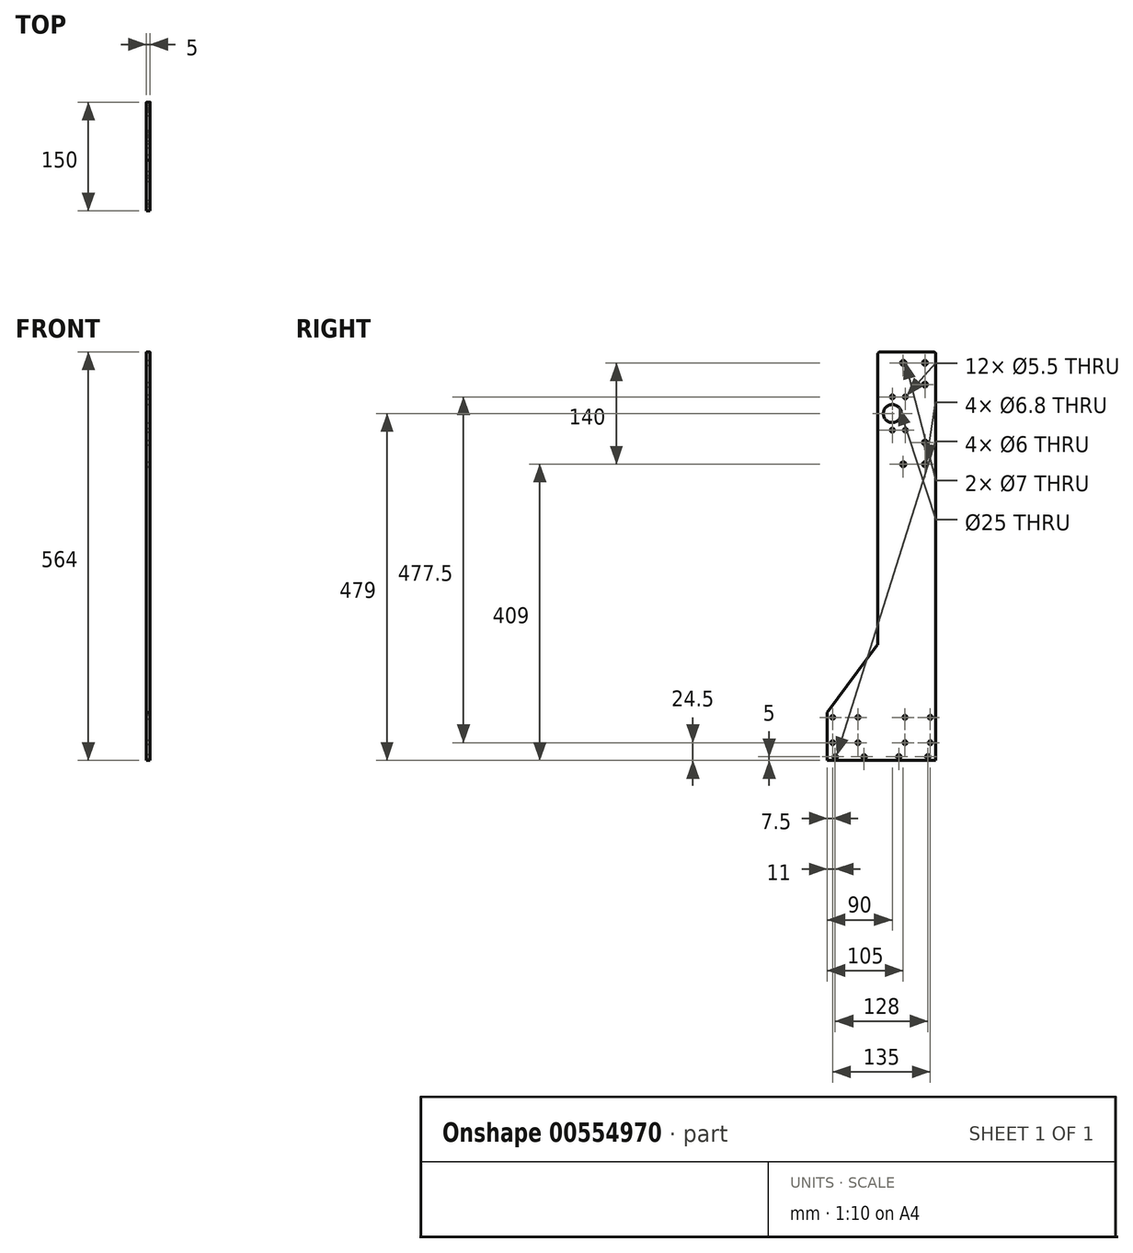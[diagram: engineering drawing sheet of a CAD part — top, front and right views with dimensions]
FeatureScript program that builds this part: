
annotation { "Feature Type Name" : "Feature", "Feature Type Description" : "" }
export const myFeature = defineFeature(function(context is Context, id is Id, definition is map)
    precondition{}
    {
        {
            var Q0;
            Q0=qCreatedBy(makeId("Right.planeOp"),FACE);
            var sketch = newSketch(context, id + "F0", { "sketchPlane" : qUnion([Q0])});
            skLineSegment(sketch, "E0.bottom", {"start": v(40, 282) * mm, "end": v(-40, 282) * mm});
            skLineSegment(sketch, "E0.top", {"start": v(40, -282) * mm, "end": v(-40, -282) * mm});
            skLineSegment(sketch, "E0.left", {"start": v(40, 282) * mm, "end": v(40, -282) * mm});
            skLineSegment(sketch, "E0.right", {"start": v(-40, 282) * mm, "end": v(-40, -122) * mm});
            skPoint(sketch, "E0.middle", {"position": v(0, 0) * mm});
            skLineSegment(sketch, "E1", {"start": v(-40, -282) * mm, "end": v(-110, -282) * mm});
            skLineSegment(sketch, "E2", {"start": v(-110, -282) * mm, "end": v(-110, -216) * mm});
            skLineSegment(sketch, "E3", {"start": v(-40, -122) * mm, "end": v(-110, -216) * mm});
            skSolve(sketch);
        }
        {
            var Q0;
            Q0=qSketchRegion(id+"F0",true);
            extrude(context, id + "F1", {"entities" : qUnion([Q0]), "endBound" : BoundingType.SYMMETRIC, "depth" : 5 * mm, "offsetDistance" : 25 * mm});
        }
        {
            var Q0;
            Q0=makeQuery(id+"F1.opExtrude","CAP_FACE",FACE,{"disambiguationData":[OSD([sQuery(id+"F0.wireOp",EDGE,"E0.bottom"),sQuery(id+"F0.wireOp",EDGE,"E0.top"),sQuery(id+"F0.wireOp",EDGE,"E0.left"),sQuery(id+"F0.wireOp",EDGE,"E0.right")])],"isStart":false});
            var sketch = newSketch(context, id + "F2", { "sketchPlane" : qUnion([Q0])});
            skCircle(sketch, "E4", {"center": v(25, 267) * mm, "radius": 3.4 * mm});
            skCircle(sketch, "E5", {"center": v(25, 237) * mm, "radius": 3.4 * mm});
            skCircle(sketch, "E6", {"center": v(25, 127) * mm, "radius": 3.4 * mm});
            skCircle(sketch, "E7", {"center": v(25, 157) * mm, "radius": 3.4 * mm});
            skCircle(sketch, "E8", {"center": v(-5, 267) * mm, "radius": 3.5 * mm});
            skCircle(sketch, "E9", {"center": v(-5, 127) * mm, "radius": 3.5 * mm});
            skCircle(sketch, "E10", {"center": v(-20, 197) * mm, "radius": 12.5 * mm});
            skPoint(sketch, "E11.center.orphan", {"position": v(-5, 237) * mm});
            skPoint(sketch, "E12.center.orphan", {"position": v(-5, 157) * mm});
            skCircle(sketch, "E13", {"center": v(-20, 220) * mm, "radius": 2.75 * mm});
            skCircle(sketch, "E14", {"center": v(-2, 220) * mm, "radius": 2.75 * mm});
            skCircle(sketch, "E15", {"center": v(-20, 174) * mm, "radius": 2.75 * mm});
            skCircle(sketch, "E16", {"center": v(-2, 174) * mm, "radius": 2.75 * mm});
            skSolve(sketch);
        }
        {
            var Q0;
            Q0=qSketchRegion(id+"F2",true);
            extrude(context, id + "F3", {"entities" : qUnion([Q0]), "operationType" : NewBodyOperationType.REMOVE, "oppositeDirection" : true, "depth" : 5 * mm, "offsetDistance" : 25 * mm});
        }
        {
            var Q0;
            Q0=makeQuery(id+"F1.opExtrude","SWEPT_EDGE",EDGE,{"disambiguationData":[OSD([sQuery(id+"F0.wireOp",EDGE,"E0.bottom"),sQuery(id+"F0.wireOp",EDGE,"E0.left")])]});
            fillet(context, id + "F4", {"entities" : qUnion([Q0]), "radius" : 3 * mm, "tangentPropagation" : true, "allowEdgeOverflow" : false});
        }
        {
            var Q0;
            Q0=makeQuery(id+"F1.opExtrude","SWEPT_EDGE",EDGE,{"disambiguationData":[OSD([sQuery(id+"F0.wireOp",EDGE,"E0.bottom"),sQuery(id+"F0.wireOp",EDGE,"E0.right")])]});
            fillet(context, id + "F5", {"entities" : qUnion([Q0]), "radius" : 3 * mm, "tangentPropagation" : true, "allowEdgeOverflow" : false});
        }
        {
            var Q0;
            Q0=makeQuery(id+"F1.opExtrude","SWEPT_EDGE",EDGE,{"disambiguationData":[OSD([sQuery(id+"F0.wireOp",EDGE,"E0.right"),sQuery(id+"F0.wireOp",EDGE,"1vJYxwGC-FJZn-p96J-PcUk-pM6sYgkwKhBf")])]});
            var Q1;
            Q1=makeQuery(id+"F1.opExtrude","SWEPT_EDGE",EDGE,{"disambiguationData":[OSD([sQuery(id+"F0.wireOp",EDGE,"1vJYxwGC-FJZn-p96J-PcUk-pM6sYgkwKhBf"),sQuery(id+"F0.wireOp",EDGE,"8exz0xhX-NDQy-IiUF-ustv-eXDvUxwHRywJ")])]});
            fillet(context, id + "F6", {"entities" : qUnion([Q0, Q1]), "radius" : 3 * mm, "tangentPropagation" : true, "allowEdgeOverflow" : false});
        }
        {
            var Q0;
            Q0=makeQuery(id+"F1.opExtrude","CAP_FACE",FACE,{"disambiguationData":[OSD([sQuery(id+"F0.wireOp",EDGE,"E0.bottom"),sQuery(id+"F0.wireOp",EDGE,"E0.top"),sQuery(id+"F0.wireOp",EDGE,"E0.left"),sQuery(id+"F0.wireOp",EDGE,"E0.right"),sQuery(id+"F0.wireOp",EDGE,"E1"),sQuery(id+"F0.wireOp",EDGE,"1vJYxwGC-FJZn-p96J-PcUk-pM6sYgkwKhBf"),sQuery(id+"F0.wireOp",EDGE,"E2"),sQuery(id+"F0.wireOp",EDGE,"8exz0xhX-NDQy-IiUF-ustv-eXDvUxwHRywJ")])],"isStart":true});
            var sketch = newSketch(context, id + "F7", { "sketchPlane" : qUnion([Q0])});
            skCircle(sketch, "E17", {"center": v(-29, -277) * mm, "radius": 3 * mm});
            skCircle(sketch, "E18", {"center": v(11, -277) * mm, "radius": 3 * mm});
            skCircle(sketch, "E19", {"center": v(59, -277) * mm, "radius": 3 * mm});
            skCircle(sketch, "E20", {"center": v(99, -277) * mm, "radius": 3 * mm});
            skSolve(sketch);
        }
        {
            var Q0;
            Q0 = qSketchRegion(id + "F7", true);
            extrude(context, id + "F8", {"entities" : qUnion([Q0]), "operationType" : NewBodyOperationType.REMOVE, "oppositeDirection" : true, "depth" : 5 * mm, "offsetDistance" : 25 * mm});
        }
        {
            var Q0;
            Q0=makeQuery(id+"F1.opExtrude","CAP_FACE",FACE,{"disambiguationData":[OSD([sQuery(id+"F0.wireOp",EDGE,"E0.bottom"),sQuery(id+"F0.wireOp",EDGE,"E0.top"),sQuery(id+"F0.wireOp",EDGE,"E0.left"),sQuery(id+"F0.wireOp",EDGE,"E0.right"),sQuery(id+"F0.wireOp",EDGE,"E1"),sQuery(id+"F0.wireOp",EDGE,"1vJYxwGC-FJZn-p96J-PcUk-pM6sYgkwKhBf"),sQuery(id+"F0.wireOp",EDGE,"E2"),sQuery(id+"F0.wireOp",EDGE,"8exz0xhX-NDQy-IiUF-ustv-eXDvUxwHRywJ")])],"isStart":true});
            var sketch = newSketch(context, id + "F9", { "sketchPlane" : qUnion([Q0])});
            skCircle(sketch, "E21", {"center": v(102.5, -222.5) * mm, "radius": 2.75 * mm});
            skCircle(sketch, "E22", {"center": v(102.5, -257.5) * mm, "radius": 2.75 * mm});
            skCircle(sketch, "E23", {"center": v(67.5, -222.5) * mm, "radius": 2.75 * mm});
            skCircle(sketch, "E24", {"center": v(67.5, -257.5) * mm, "radius": 2.75 * mm});
            skCircle(sketch, "E25", {"center": v(-32.5, -222.5) * mm, "radius": 2.75 * mm});
            skCircle(sketch, "E26", {"center": v(2.5, -222.5) * mm, "radius": 2.75 * mm});
            skCircle(sketch, "E27", {"center": v(-32.5, -257.5) * mm, "radius": 2.75 * mm});
            skCircle(sketch, "E28", {"center": v(2.5, -257.5) * mm, "radius": 2.75 * mm});
            skSolve(sketch);
        }
        {
            var Q0;
            Q0 = qSketchRegion(id + "F9", true);
            extrude(context, id + "F10", {"entities" : qUnion([Q0]), "operationType" : NewBodyOperationType.REMOVE, "oppositeDirection" : true, "depth" : 5 * mm, "offsetDistance" : 25 * mm});
        }
    });
